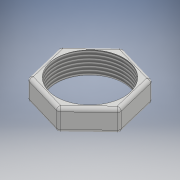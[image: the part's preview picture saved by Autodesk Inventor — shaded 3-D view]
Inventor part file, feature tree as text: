
AUTODESK INVENTOR PART (.ipt)
format: ipt  version: 2017 (Build 210142000, 142)  size: 142,848 bytes
history: native  units: mm
features: sketch x2, extrude x1, thread x1, fillet x1
ambient origin geometry x8: Origin, YZ Plane, XZ Plane, XY Plane, X Axis, Y Axis, Z Axis, Center Point
bodies: Solid1 (feature_tree)
feature tree (5):
  extrude  "Extrusion1"  Depth=10.0mm TaperAngle=0.0deg
  sketch  "3D Sketch1"
  thread  "Thread1"  [1 undecoded]
  fillet  "Fillet1"  [1 undecoded]
  sketch  "Sketch1"  dims[d0=20.0mm d1=0.0mm d2=10.0mm d3=0.0mm d4=3.0mm]
note: 2 required parameter values undecoded (feature->parameter linkage not recoverable at this tier; creation-order binding heuristic only, values carry confidence <= 0.55)
